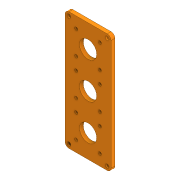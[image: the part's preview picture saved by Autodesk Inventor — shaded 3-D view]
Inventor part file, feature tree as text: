
AUTODESK INVENTOR PART (.ipt)
format: ipt  version: 2020 (Build 240168000, 168)  size: 916,480 bytes
history: native  units: in
note: dims shown in document units (in); Inventor stores cm internally (conversion verified against a paired STEP export)
features: sketch x24, chamfer x23, extrude x21, projected_geometry x11, plane x3, loft x2, fillet x1, other x1
ambient origin geometry x8: Origin, YZ Plane, XZ Plane, XY Plane, X Axis, Y Axis, Z Axis, Center Point
bodies: Solid1 (feature_tree)
feature tree (86):
  extrude  "Extrusion1"  Depth=2.3622in
  extrude  "Extrusion2"  Depth=1.6535in
  chamfer  "Chamfer1"  Distance=0.5512in
  extrude  "Extrusion3"  Depth=0.0157in
  extrude  "Extrusion4"  Depth=0.2756in TaperAngle=0.0deg
  extrude  "Extrusion5"  Depth=0.315in
  extrude  "Extrusion6"  Depth=0.4724in
  extrude  "Extrusion7"  Depth=0.0787in
  plane  "Work Plane1"
  extrude  "Extrusion8"  Depth=0.0984in
  plane  "Work Plane2"
  extrude  "Extrusion9"  Depth=1.0994in
  sketch  "Sketch11"  dims[d31=15.0deg d32=0.4921in d33=0.0in]
  plane  "Work Plane3"
  extrude  "Extrusion10"  Depth=0.4921in TaperAngle=0.0deg
  extrude  "Extrusion11"  Depth=1.5748in TaperAngle=360.0deg
  loft  "Loft1"
  loft  "Loft2"
  sketch  "Sketch16"  dims[d47=0.315in d48=0.4331in]
  extrude  "Extrusion12"  Depth=0.0984in TaperAngle=0.0deg
  extrude  "Extrusion13"  Depth=0.4331in
  extrude  "Extrusion14"  Depth=0.0984in
  extrude  "Extrusion15"  Depth=0.0984in
  chamfer  "Chamfer2"  Distance=0.0984in
  chamfer  "Chamfer3"  Distance=1.6654in
  chamfer  "Chamfer4"  Distance=0.1969in
  chamfer  "Chamfer5"  Distance=0.1969in
  chamfer  "Chamfer6"  Distance=0.3484in
  chamfer  "Chamfer7"  Distance=0.3484in
  chamfer  "Chamfer8"  Distance=0.1969in
  chamfer  "Chamfer9"  Distance=0.1969in
  chamfer  "Chamfer10"  Distance=0.1969in
  chamfer  "Chamfer11"  Distance=0.3937in
  chamfer  "Chamfer12"  Distance=0.7874in
  chamfer  "Chamfer13"  Angle=90.0deg  [1 undecoded]
  chamfer  "Chamfer14"  Angle=90.0deg  [1 undecoded]
  chamfer  "Chamfer15"  Angle=90.0deg  [1 undecoded]
  chamfer  "Chamfer16"  Angle=90.0deg  [1 undecoded]
  chamfer  "Chamfer17"  Distance=0.7874in
  chamfer  "Chamfer18"  Distance=0.3937in
  chamfer  "Chamfer19"  Distance=0.3937in
  chamfer  "Chamfer20"  Distance=0.7874in
  chamfer  "Chamfer21"  Distance=0.1969in
  chamfer  "Chamfer22"  Distance=0.8858in
  fillet  "Fillet1"  Radius=1.6654in
  chamfer  "Chamfer23"  Distance=1.6654in
  extrude  "Extrusion19"  TaperAngle=0.0deg  [1 undecoded]
  extrude  "Extrusion20"  TaperAngle=0.0deg  [1 undecoded]
  extrude  "Extrusion21"  Depth=0.1181in
  extrude  "Extrusion22"  Depth=0.1181in
  extrude  "Extrusion23"  Depth=0.1181in
  extrude  "Extrusion24"  Depth=0.1181in
  sketch  "Sketch1"  dims[d0=2.3622in d1=2.0472in]
  sketch  "Sketch2"  dims[d2=0.2756in d3=0.0in d4=1.6535in d5=0.5512in d6=0.0in]
  sketch  "Sketch3"  dims[d7=0.2756in d8=0.125in d9=0.0137in d10=0.0157in]
  sketch  "Sketch5"  dims[d11=4.7244in d13=360.0deg d15=0.2756in d16=0.0in]
  sketch  "Sketch6"  dims[d17=0.5512in d19=0.315in]
  projected_geometry  "Projected Loop1"
  sketch  "Sketch7"  dims[d20=0.315in d21=0.4724in]
  projected_geometry  "Projected Loop2"
  sketch  "Sketch8"  dims[d22=0.4724in d23=0.0787in d24=0.0787in d25=0.0787in]
  projected_geometry  "Projected Loop3"
  sketch  "Sketch9"  dims[d26=0.0984in d27=0.0in d28=0.1575in]
  sketch  "Sketch10"  dims[d29=0.1575in d30=1.0994in]
  sketch  "Sketch12"  dims[d34=1.4567in d35=0.0in d36=1.5748in d38=360.0deg]
  sketch  "Sketch13"  dims[d40=0.0787in d41=0.0787in]
  projected_geometry  "Projected Loop4"
  other  "Edges1"
  sketch  "Sketch14"  dims[d42=0.0787in d43=0.0787in]
  projected_geometry  "Projected Loop5"
  sketch  "Sketch15"  dims[d44=0.0787in d45=0.0984in d46=0.0in]
  projected_geometry  "Projected Loop6"
  projected_geometry  "Projected Loop7"
  sketch  "Sketch19"  dims[d49=0.0984in d50=0.0in d51=0.6161in]
  projected_geometry  "Projected Loop8"
  sketch  "Sketch20"  dims[d52=0.1575in d53=0.1575in d54=0.0984in d55=0.0in]
  projected_geometry  "Projected Loop9"
  sketch  "Sketch21"  dims[d56=6.6929in]
  sketch  "Sketch25"  dims[d57=0.8858in]
  sketch  "Sketch26"  dims[d58=1.6654in]
  projected_geometry  "Projected Loop11"
  sketch  "Sketch27"  dims[d59=1.6654in]
  projected_geometry  "Projected Loop12"
  sketch  "Sketch28"  dims[d60=0.0in]
  sketch  "Sketch29"  dims[d61=0.0in]
  sketch  "Sketch30"  dims[d62=1.6654in d63=1.6654in d64=0.1969in d65=0.1969in d66=0.3484in d67=0.3484in d68=0.1969in d69=0.1969in d70=0.1969in d71=0.3937in d72=0.0in d73=0.7874in d74=0.0in d75=0.0in d76=90.0deg d77=0.0in d78=90.0deg d79=0.0in d80=90.0deg d81=0.0in d82=90.0deg d86=0.7874in d87=0.0in d90=0.3937in d91=0.3937in d92=0.7874in d93=0.0in d94=0.1969in d95=0.0in d96=0.8858in d97=1.6654in d98=1.6654in d99=0.0in d100=0.0in d101=0.2224in d102=0.1575in d103=0.1575in d104=0.1575in d105=0.1575in d106=0.0984in d107=0.0984in d108=0.1969in d109=0.0in d122=0.1575in d123=0.0787in d124=45.0deg d125=0.0787in d126=0.1575in d127=45.0deg d128=0.1575in d129=0.0787in d130=45.0deg d131=0.0787in d132=0.1575in d133=45.0deg d134=0.1575in d135=0.0787in d136=45.0deg d137=0.1575in d138=0.0787in d139=45.0deg d140=0.1575in d141=0.0787in d142=45.0deg d143=0.1575in d144=0.0787in d145=45.0deg d146=0.0787in d147=0.1575in d148=45.0deg d149=0.1575in d150=0.0787in d151=45.0deg d152=0.1575in d153=0.0787in d154=45.0deg d155=0.0787in d156=0.1575in d157=45.0deg d158=0.0591in d159=0.1575in d160=0.0137in d161=0.0591in d162=0.1575in d163=0.0137in d164=0.0591in d165=0.1575in d166=0.0137in d167=0.0591in d168=0.1575in d169=0.0137in d170=0.0591in d171=0.1575in d172=0.0137in d173=0.0591in d174=0.1575in d175=0.0137in d176=0.0591in d177=0.1575in d178=0.0137in d179=0.0591in d180=0.1575in d181=0.0137in d182=0.0591in d183=0.1575in d184=0.0137in d185=0.0197in d193=0.0984in d194=0.3937in d195=0.125in d196=45.0deg d197=0.2756in d198=0.1969in d199=0.0in d200=0.2756in d201=2.7559in d202=0.2756in d203=0.2756in d204=0.2756in d205=0.2756in d206=0.2756in d207=0.2756in d208=0.2756in d209=0.0394in d210=0.2047in d211=0.0in d212=0.1969in d213=0.2756in d214=0.0in d215=0.0in d216=0.0in d217=0.1969in d218=0.1969in d219=0.1969in d220=0.1969in d221=1.0in d222=0.0in d223=0.2953in d224=0.2953in d225=0.2953in d226=0.2953in d227=0.1181in d228=0.0in]
note: 6 required parameter values undecoded (feature->parameter linkage not recoverable at this tier; creation-order binding heuristic only, values carry confidence <= 0.55)
